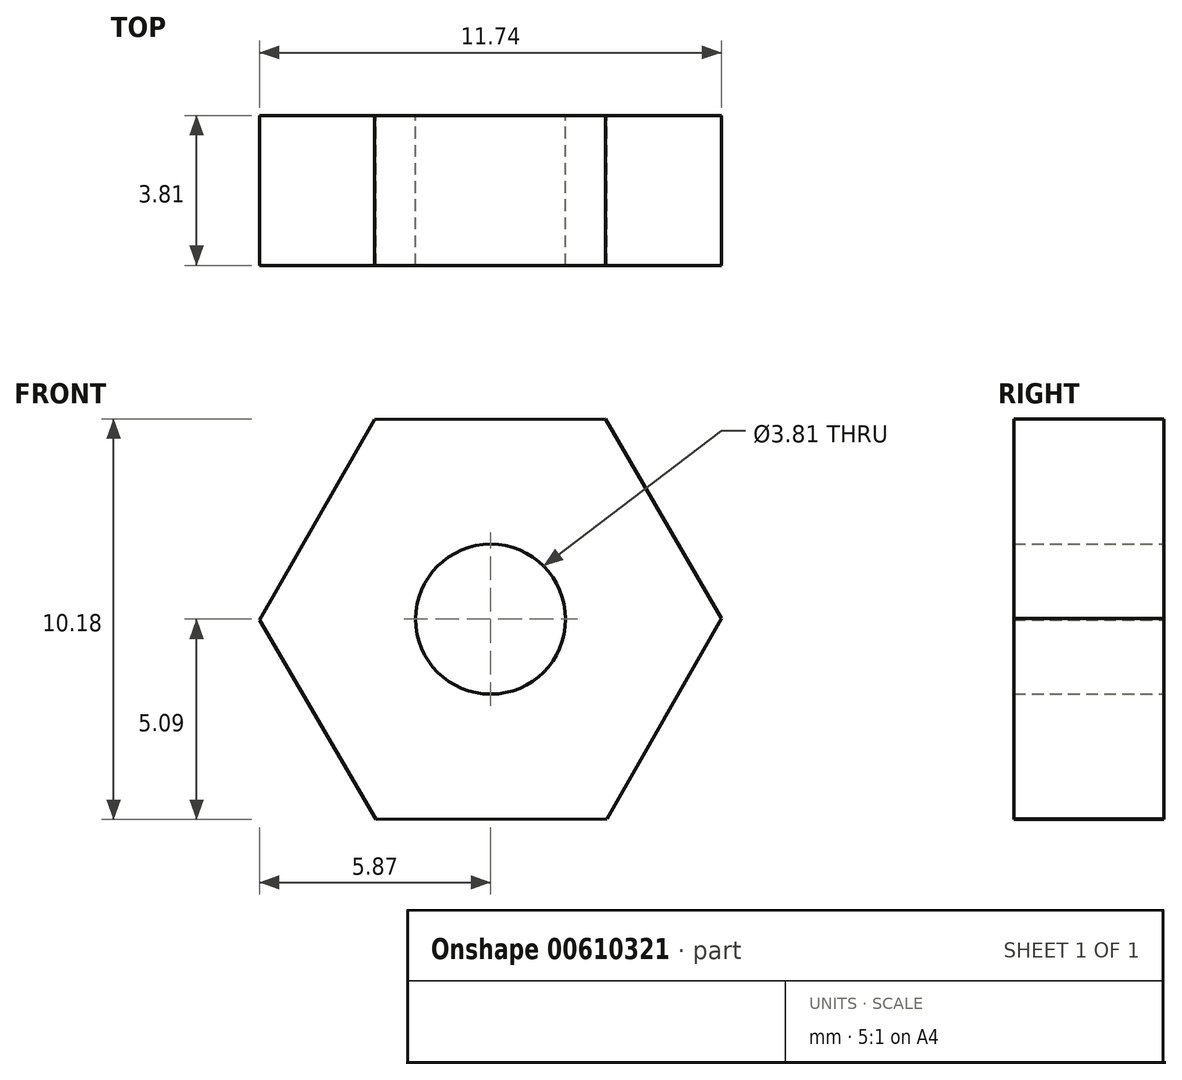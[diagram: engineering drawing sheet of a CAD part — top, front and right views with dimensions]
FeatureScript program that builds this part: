
annotation { "Feature Type Name" : "Feature", "Feature Type Description" : "" }
export const myFeature = defineFeature(function(context is Context, id is Id, definition is map)
    precondition{}
    {
        {
            var Q0;
            Q0=qCreatedBy(makeId("Front.planeOp"),FACE);
            var sketch = newSketch(context, id + "F0", { "sketchPlane" : qUnion([Q0])});
            skCircle(sketch, "E0.cCircle", {"center": v(0, 0) * mm, "radius": 5.08 * mm, "construction": true});
            skLineSegment(sketch, "E0.0", {"start": v(2.91, 5.1) * mm, "end": v(5.87, 0.02) * mm});
            skLineSegment(sketch, "E0.1", {"start": v(5.87, 0.02) * mm, "end": v(2.95, -5.07) * mm});
            skLineSegment(sketch, "E0.2", {"start": v(2.95, -5.07) * mm, "end": v(-2.91, -5.1) * mm});
            skLineSegment(sketch, "E0.3", {"start": v(-2.91, -5.1) * mm, "end": v(-5.87, -0.02) * mm});
            skLineSegment(sketch, "E0.4", {"start": v(-5.87, -0.02) * mm, "end": v(-2.95, 5.07) * mm});
            skLineSegment(sketch, "E0.5", {"start": v(-2.95, 5.07) * mm, "end": v(2.91, 5.1) * mm});
            skPoint(sketch, "E0.0.midPoint", {"position": v(4.39, 2.56) * mm});
            skCircle(sketch, "E1", {"center": v(0, 0) * mm, "radius": 1.9 * mm});
            skSolve(sketch);
        }
        {
            var Q0;
            Q0 = qSketchRegion(id + "F0", true);
            extrude(context, id + "F1", {"entities" : qUnion([Q0]), "depth" : 3.8 * mm, "offsetDistance" : 25.4 * mm});
        }
    });
